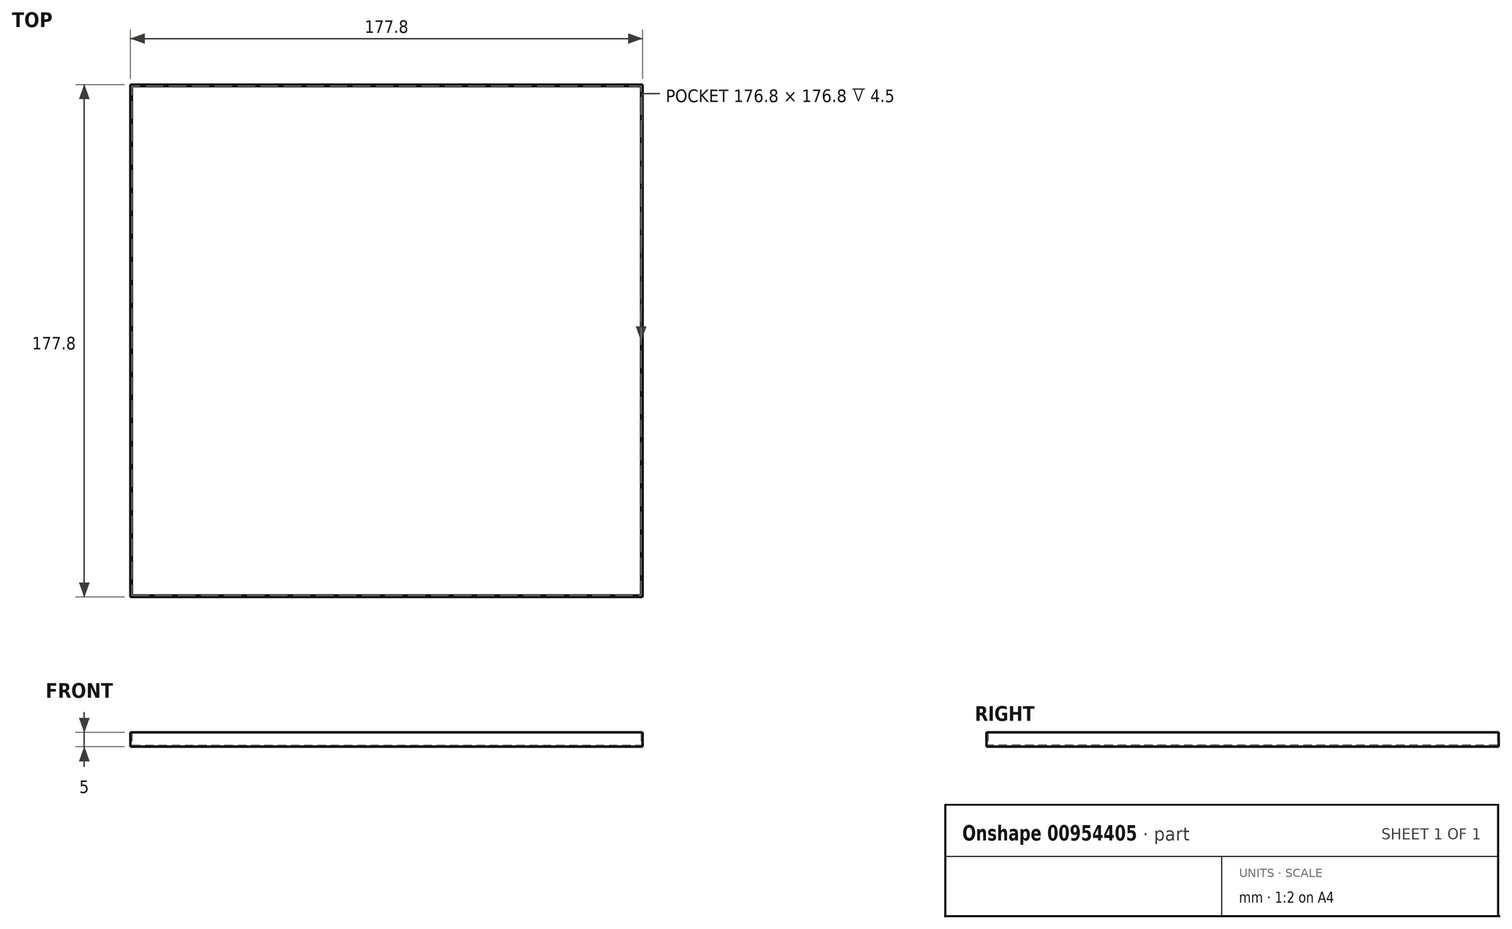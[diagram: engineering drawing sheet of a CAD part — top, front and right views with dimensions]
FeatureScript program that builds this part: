
annotation { "Feature Type Name" : "Feature", "Feature Type Description" : "" }
export const myFeature = defineFeature(function(context is Context, id is Id, definition is map)
    precondition{}
    {
        {
            assignVariable(context, id + "F0", {"name" : "tykkelse", "anyValue" : .5});
        }
        {
            var Q0;
            Q0=qCreatedBy(makeId("Top.planeOp"),FACE);
            var sketch = newSketch(context, id + "F1", { "sketchPlane" : qUnion([Q0])});
            skLineSegment(sketch, "E0.bottom", {"start": v(-125.92, 85.92) * mm, "end": v(51.88, 85.92) * mm});
            skLineSegment(sketch, "E0.top", {"start": v(-125.92, -91.88) * mm, "end": v(51.88, -91.88) * mm});
            skLineSegment(sketch, "E0.left", {"start": v(-125.92, 85.92) * mm, "end": v(-125.92, -91.88) * mm});
            skLineSegment(sketch, "E0.right", {"start": v(51.88, 85.92) * mm, "end": v(51.88, -91.88) * mm});
            skSolve(sketch);
        }
        {
            assignVariable(context, id + "F2", {"name" : "hoyde", "anyValue" : 5});
        }
        {
            var Q0;
            Q0=makeQuery(id+"F1.imprint","IMPRINT",FACE,{"disambiguationData":[TD([[makeQuery(id+"F1.imprint","IMPRINT",EDGE,{"derivedFrom":sQuery(id+"F1.wireOp",EDGE,"E0.bottom")}),-1.0]])]});
            extrude(context, id + "F3", {"entities" : qUnion([Q0]), "depth" : (getVariable(context, 'hoyde')) * mm, "offsetDistance" : 25.4 * mm});
        }
        {
            var Q0;
            Q0=makeQuery(id+"F3.opExtrude","CAP_FACE",FACE,{"disambiguationData":[OSD([sQuery(id+"F1.wireOp",EDGE,"E0.bottom"),sQuery(id+"F1.wireOp",EDGE,"E0.top"),sQuery(id+"F1.wireOp",EDGE,"E0.left"),sQuery(id+"F1.wireOp",EDGE,"E0.right")])],"isStart":false});
            shell(context, id + "F4", {"entities" : qUnion([Q0]), "thickness" : (getVariable(context, 'tykkelse')) * mm});
        }
    });
